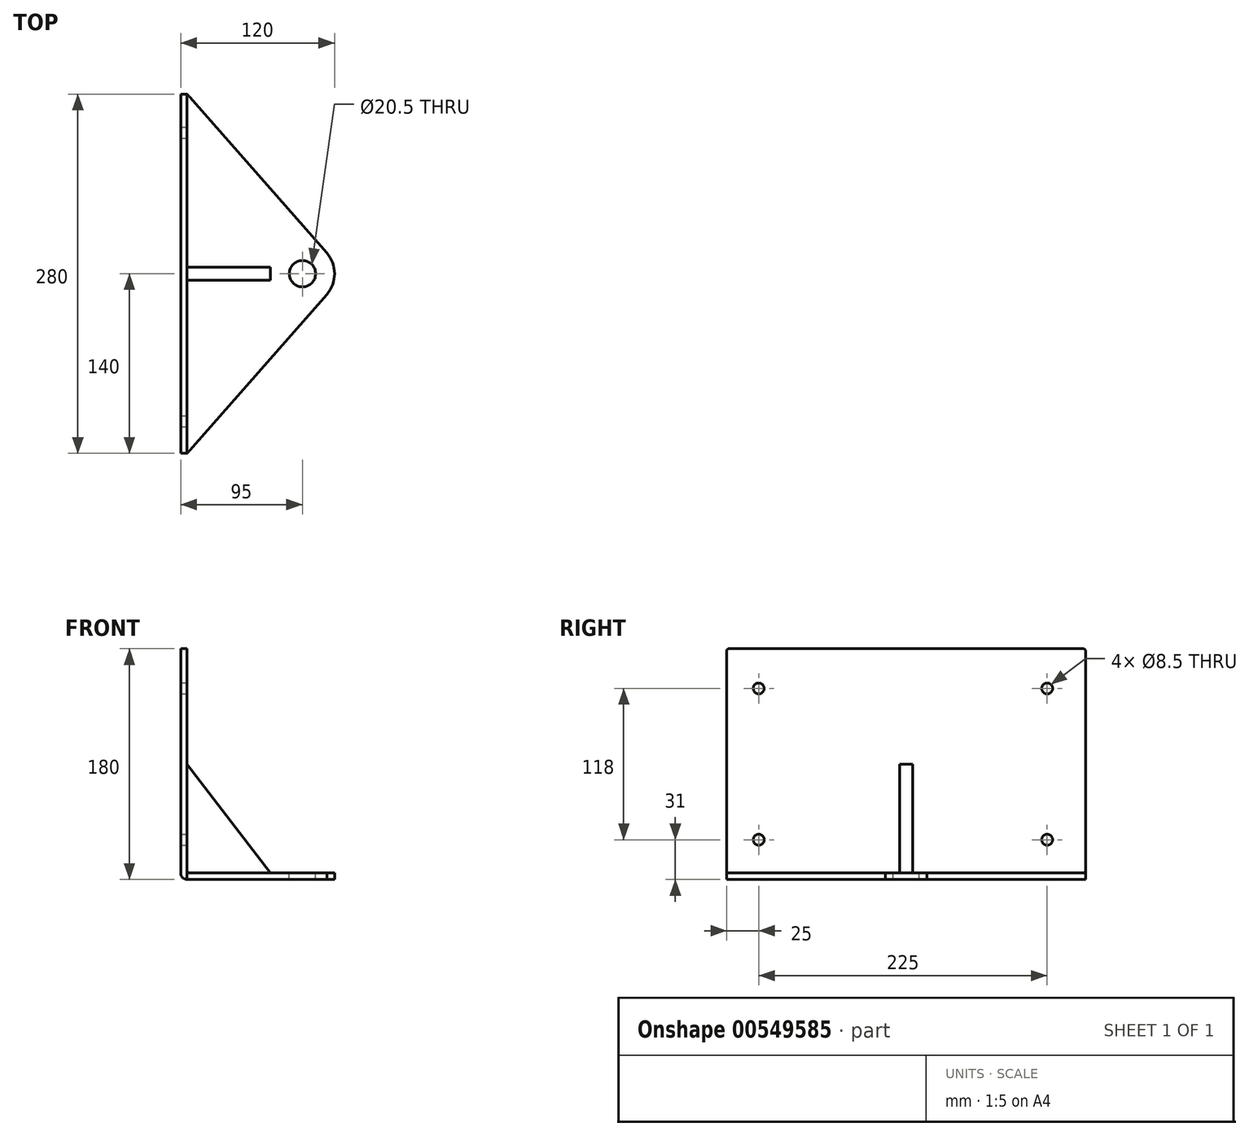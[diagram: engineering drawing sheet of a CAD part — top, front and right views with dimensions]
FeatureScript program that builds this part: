
annotation { "Feature Type Name" : "Feature", "Feature Type Description" : "" }
export const myFeature = defineFeature(function(context is Context, id is Id, definition is map)
    precondition{}
    {
        {
            var Q0;
            Q0=qCreatedBy(makeId("Front.planeOp"),FACE);
            var sketch = newSketch(context, id + "F0", { "sketchPlane" : qUnion([Q0])});
            skLineSegment(sketch, "E0", {"start": v(-5, 87.5) * mm, "end": v(-5, -92.5) * mm});
            skLineSegment(sketch, "E1", {"start": v(-5, -92.5) * mm, "end": v(115, -92.5) * mm});
            skLineSegment(sketch, "E2", {"start": v(115, -92.5) * mm, "end": v(115, -87.5) * mm});
            skLineSegment(sketch, "E3", {"start": v(115, -87.5) * mm, "end": v(0, -87.5) * mm});
            skLineSegment(sketch, "E4", {"start": v(0, -87.5) * mm, "end": v(0, 87.5) * mm});
            skLineSegment(sketch, "E5", {"start": v(0, 87.5) * mm, "end": v(-5, 87.5) * mm});
            skSolve(sketch);
        }
        {
            var Q0;
            Q0=makeQuery(id+"F0.imprint","IMPRINT",FACE,{"disambiguationData":[TD([[makeQuery(id+"F0.imprint","IMPRINT",EDGE,{"derivedFrom":sQuery(id+"F0.wireOp",EDGE,"E0")}),1.0]])]});
            extrude(context, id + "F1", {"entities" : qUnion([Q0]), "oppositeDirection" : true, "depth" : 280 * mm, "offsetDistance" : 25 * mm});
        }
        {
            var Q0;
            Q0=makeQuery(id+"F1.opExtrude","CAP_EDGE",EDGE,{"disambiguationData":[OSD([sQuery(id+"F0.wireOp",EDGE,"E5")])],"isStart":false});
            var Q1;
            Q1=makeQuery(id+"F1.opExtrude","CAP_EDGE",EDGE,{"disambiguationData":[OSD([sQuery(id+"F0.wireOp",EDGE,"E5")])],"isStart":true});
            fillet(context, id + "F2", {"entities" : qUnion([Q0, Q1]), "radius" : 2 * mm, "tangentPropagation" : true, "allowEdgeOverflow" : false});
        }
        {
            var Q0;
            Q0=makeQuery(id+"F1.opExtrude","SWEPT_FACE",FACE,{"disambiguationData":[OSD([sQuery(id+"F0.wireOp",EDGE,"E4")])]});
            var sketch = newSketch(context, id + "F3", { "sketchPlane" : qUnion([Q0])});
            skLineSegment(sketch, "E6", {"start": v(-73.13, 56.5) * mm, "end": v(342.86, 56.5) * mm, "construction": true});
            skLineSegment(sketch, "E7", {"start": v(-75.7, -61.5) * mm, "end": v(355.26, -61.5) * mm, "construction": true});
            skLineSegment(sketch, "E8", {"start": v(250, 114.73) * mm, "end": v(250, -108.7) * mm, "construction": true});
            skLineSegment(sketch, "E9", {"start": v(25, 119.04) * mm, "end": v(25, -107.27) * mm, "construction": true});
            skCircle(sketch, "E10", {"center": v(25, 56.5) * mm, "radius": 4.25 * mm});
            skCircle(sketch, "E11", {"center": v(25, -61.5) * mm, "radius": 4.25 * mm});
            skCircle(sketch, "E12", {"center": v(250, 56.5) * mm, "radius": 4.25 * mm});
            skCircle(sketch, "E13", {"center": v(250, -61.5) * mm, "radius": 4.25 * mm});
            skSolve(sketch);
        }
        {
            var Q0;
            Q0=makeQuery(id+"F3.imprint","IMPRINT",FACE,{"disambiguationData":[TD([[makeQuery(id+"F3.imprint","IMPRINT",EDGE,{"derivedFrom":sQuery(id+"F3.wireOp",EDGE,"E10")}),1.0]])]});
            var Q1;
            Q1=makeQuery(id+"F3.imprint","IMPRINT",FACE,{"disambiguationData":[TD([[makeQuery(id+"F3.imprint","IMPRINT",EDGE,{"derivedFrom":sQuery(id+"F3.wireOp",EDGE,"E11")}),1.0]])]});
            var Q2;
            Q2=makeQuery(id+"F3.imprint","IMPRINT",FACE,{"disambiguationData":[TD([[makeQuery(id+"F3.imprint","IMPRINT",EDGE,{"derivedFrom":sQuery(id+"F3.wireOp",EDGE,"E13")}),1.0]])]});
            var Q3;
            Q3=makeQuery(id+"F3.imprint","IMPRINT",FACE,{"disambiguationData":[TD([[makeQuery(id+"F3.imprint","IMPRINT",EDGE,{"derivedFrom":sQuery(id+"F3.wireOp",EDGE,"E12")}),1.0]])]});
            extrude(context, id + "F4", {"entities" : qUnion([Q0, Q1, Q2, Q3]), "operationType" : NewBodyOperationType.REMOVE, "endBound" : BoundingType.THROUGH_ALL, "oppositeDirection" : true, "depth" : 25 * mm, "offsetDistance" : 25 * mm});
        }
        {
            var Q0;
            Q0=makeQuery(id+"F1.opExtrude","SWEPT_FACE",FACE,{"disambiguationData":[OSD([sQuery(id+"F0.wireOp",EDGE,"E4")])]});
            var sketch = newSketch(context, id + "F5", { "sketchPlane" : qUnion([Q0])});
            skLineSegment(sketch, "E14", {"start": v(-137.2, -2.5) * mm, "end": v(394.4, -2.5) * mm, "construction": true});
            skLineSegment(sketch, "E15.bottom", {"start": v(135, -2.5) * mm, "end": v(145, -2.5) * mm});
            skLineSegment(sketch, "E15.top", {"start": v(135, -87.5) * mm, "end": v(145, -87.5) * mm});
            skLineSegment(sketch, "E15.left", {"start": v(135, -2.5) * mm, "end": v(135, -87.5) * mm});
            skLineSegment(sketch, "E15.right", {"start": v(145, -2.5) * mm, "end": v(145, -87.5) * mm});
            skSolve(sketch);
        }
        {
            var Q0;
            Q0=makeQuery(id+"F5.imprint","IMPRINT",FACE,{"disambiguationData":[TD([[makeQuery(id+"F5.imprint","IMPRINT",EDGE,{"derivedFrom":sQuery(id+"F5.wireOp",EDGE,"E15.bottom")}),-1.0]])]});
            extrude(context, id + "F6", {"entities" : qUnion([Q0]), "operationType" : NewBodyOperationType.ADD, "depth" : 65 * mm, "offsetDistance" : 25 * mm});
        }
        {
            var Q0;
            Q0=makeQuery(id+"F6.opExtrude","SWEPT_FACE",FACE,{"disambiguationData":[OSD([sQuery(id+"F5.wireOp",EDGE,"E15.right")])]});
            var sketch = newSketch(context, id + "F7", { "sketchPlane" : qUnion([Q0])});
            skLineSegment(sketch, "E16", {"start": v(0, -2.5) * mm, "end": v(-65, -87.5) * mm});
            skSolve(sketch);
        }
        {
            var Q0;
            Q0=makeQuery(id+"F7.imprint","IMPRINT",FACE,{"disambiguationData":[TD([[makeQuery(id+"F7.imprint","IMPRINT",EDGE,{"derivedFrom":sQuery(id+"F7.wireOp",EDGE,"E16")}),-1.0]])]});
            extrude(context, id + "F8", {"entities" : qUnion([Q0]), "operationType" : NewBodyOperationType.REMOVE, "endBound" : BoundingType.THROUGH_ALL, "oppositeDirection" : true, "depth" : 25 * mm, "offsetDistance" : 25 * mm});
        }
        {
            var Q0;
            Q0=makeQuery(id+"F1.opExtrude","SWEPT_FACE",FACE,{"disambiguationData":[OSD([sQuery(id+"F0.wireOp",EDGE,"E3")])]});
            var sketch = newSketch(context, id + "F9", { "sketchPlane" : qUnion([Q0])});
            skLineSegment(sketch, "E17", {"start": v(90, -36.76) * mm, "end": v(90, 302.18) * mm, "construction": true});
            skLineSegment(sketch, "E18", {"start": v(180.96, 140) * mm, "end": v(-158.25, 140) * mm, "construction": true});
            skArc(sketch, "E19", {"start": v(109.14, 123.92) * mm, "mid": v(115, 140) * mm, "end": v(109.14, 156.08) * mm});
            skCircle(sketch, "E20", {"center": v(90, 140) * mm, "radius": 10.25 * mm});
            skLineSegment(sketch, "E21", {"start": v(109.14, 156.08) * mm, "end": v(0, 280) * mm});
            skLineSegment(sketch, "E22", {"start": v(109.14, 123.92) * mm, "end": v(0, 0) * mm});
            skSolve(sketch);
        }
        {
            var Q0;
            {var subQ0=sQuery(id+"F9.wireOp",EDGE,"XeAGc9ni-2kSY-L14J-L4Wf-9UhgiyoOZcCi");Q0=makeQuery(id+"F9.imprint","IMPRINT",FACE,{"disambiguationData":[TD([[makeQuery(id+"F9.imprint","IMPRINT",EDGE,{"derivedFrom":subQ0}),-1.0]])]});}
            var Q1;
            {var subQ0=sQuery(id+"F9.wireOp",EDGE,"Nh2j9WTP-Xldk-xG4m-SWLM-j4ZXN4M92TMK");Q1=makeQuery(id+"F9.imprint","IMPRINT",FACE,{"disambiguationData":[TD([[makeQuery(id+"F9.imprint","IMPRINT",EDGE,{"derivedFrom":subQ0}),1.0]])]});}
            var Q2;
            Q2=makeQuery(id+"F9.imprint","IMPRINT",FACE,{"disambiguationData":[TD([[makeQuery(id+"F9.imprint","IMPRINT",EDGE,{"derivedFrom":sQuery(id+"F9.wireOp",EDGE,"E20")}),1.0]])]});
            var Q3;
            {var subQ0=sQuery(id+"F9.wireOp",EDGE,"E21");Q3=makeQuery(id+"F9.imprint","IMPRINT",FACE,{"disambiguationData":[TD([[makeQuery(id+"F9.imprint","IMPRINT",EDGE,{"derivedFrom":subQ0}),-1.0]])]});}
            var Q4;
            {var subQ0=sQuery(id+"F9.wireOp",EDGE,"E22");Q4=makeQuery(id+"F9.imprint","IMPRINT",FACE,{"disambiguationData":[TD([[makeQuery(id+"F9.imprint","IMPRINT",EDGE,{"derivedFrom":subQ0}),1.0]])]});}
            extrude(context, id + "F10", {"entities" : qUnion([Q0, Q1, Q2, Q3, Q4]), "operationType" : NewBodyOperationType.REMOVE, "endBound" : BoundingType.THROUGH_ALL, "oppositeDirection" : true, "depth" : 25 * mm, "offsetDistance" : 25 * mm});
        }
        {
            var Q0;
            Q0=makeQuery(id+"F1.opExtrude","SWEPT_EDGE",EDGE,{"disambiguationData":[OSD([sQuery(id+"F0.wireOp",EDGE,"E0"),sQuery(id+"F0.wireOp",EDGE,"E1")])]});
            fillet(context, id + "F11", {"entities" : qUnion([Q0]), "radius" : 5 * mm, "tangentPropagation" : true, "allowEdgeOverflow" : false});
        }
        {
            var Q0;
            {var subQ0=sQuery(id+"F0.wireOp",EDGE,"E4");var subQ1=sQuery(id+"F0.wireOp",EDGE,"E3");Q0=makeQuery(id+"F6.boolean.opBoolean","SPLIT",EDGE,{"disambiguationData":[TD([makeQuery(id+"F6.opExtrude","SWEPT_FACE",FACE,{"disambiguationData":[OSD([sQuery(id+"F5.wireOp",EDGE,"E15.right")])]})])],"derivedFrom":makeQuery(id+"F1.opExtrude","SWEPT_EDGE",EDGE,{"disambiguationData":[OSD([subQ1,subQ0])]})});}
            var Q1;
            {var subQ0=sQuery(id+"F0.wireOp",EDGE,"E4");var subQ1=sQuery(id+"F0.wireOp",EDGE,"E3");Q1=makeQuery(id+"F6.boolean.opBoolean","SPLIT",EDGE,{"disambiguationData":[TD([makeQuery(id+"F6.opExtrude","SWEPT_FACE",FACE,{"disambiguationData":[OSD([sQuery(id+"F5.wireOp",EDGE,"E15.left")])]})])],"derivedFrom":makeQuery(id+"F1.opExtrude","SWEPT_EDGE",EDGE,{"disambiguationData":[OSD([subQ1,subQ0])]})});}
            fillet(context, id + "F12", {"entities" : qUnion([Q0, Q1]), "radius" : 2 * mm, "tangentPropagation" : true, "allowEdgeOverflow" : false});
        }
    });
